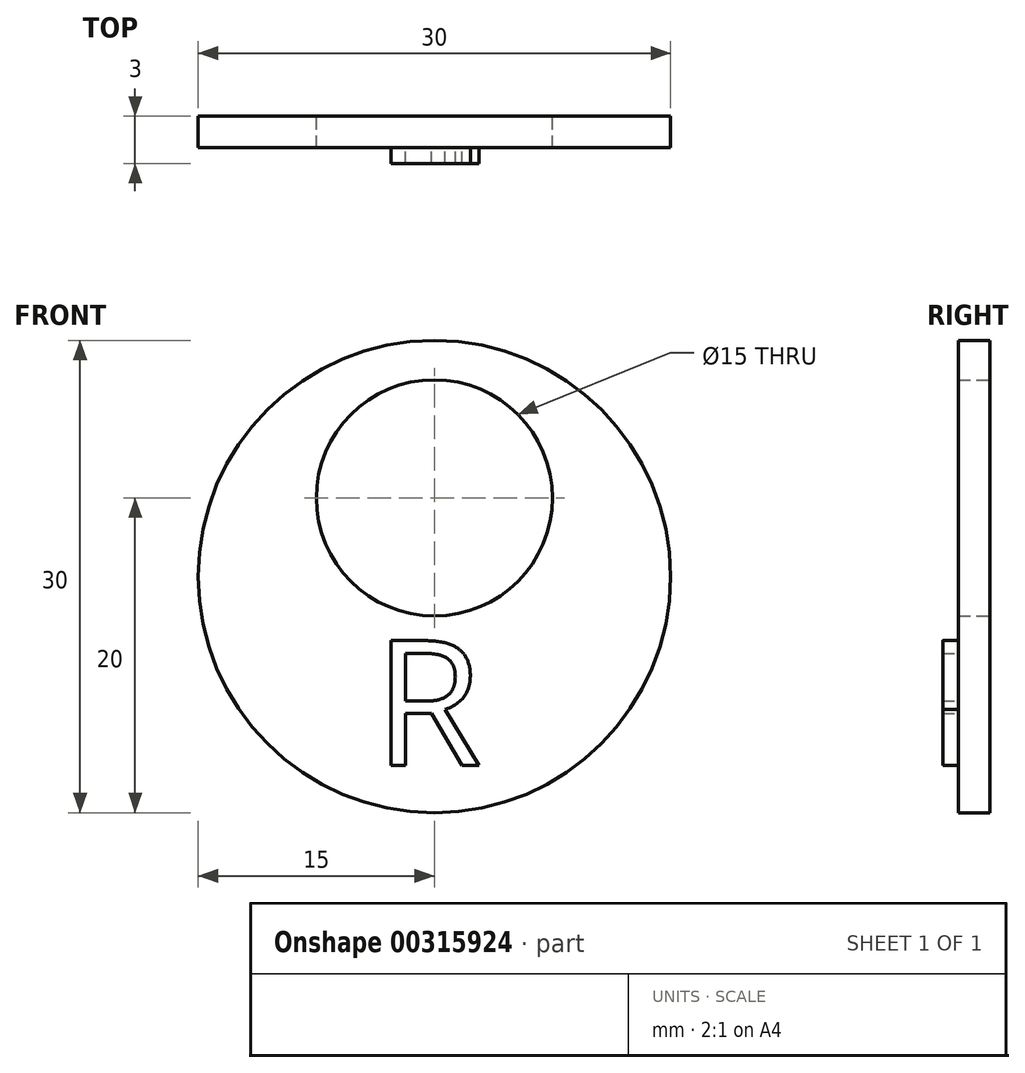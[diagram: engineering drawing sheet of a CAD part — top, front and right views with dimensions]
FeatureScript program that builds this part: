
annotation { "Feature Type Name" : "Feature", "Feature Type Description" : "" }
export const myFeature = defineFeature(function(context is Context, id is Id, definition is map)
    precondition{}
    {
        {
            var Q0;
            Q0=qCreatedBy(makeId("Front.planeOp"),FACE);
            var sketch = newSketch(context, id + "F0", { "sketchPlane" : qUnion([Q0])});
            skCircle(sketch, "E0", {"center": v(0, 0) * mm, "radius": 15 * mm});
            skPoint(sketch, "E1", {"position": v(0, 5) * mm});
            skCircle(sketch, "E2", {"center": v(0, 5) * mm, "radius": 7.5 * mm});
            skSolve(sketch);
        }
        {
            var Q0;
            Q0=makeQuery(id+"F0.imprint","IMPRINT",FACE,{"disambiguationData":[TD([[makeQuery(id+"F0.imprint","IMPRINT",EDGE,{"derivedFrom":sQuery(id+"F0.wireOp",EDGE,"E0")}),1.0]])]});
            extrude(context, id + "F1", {"entities" : qUnion([Q0]), "depth" : 2 * mm});
        }
        {
            var Q0;
            Q0=makeQuery(id+"F1.opExtrude","CAP_FACE",FACE,{"disambiguationData":[OSD([sQuery(id+"F0.wireOp",EDGE,"E0"),sQuery(id+"F0.wireOp",EDGE,"E2")])],"isStart":false});
            var sketch = newSketch(context, id + "F2", { "sketchPlane" : qUnion([Q0])});
            skText(sketch, "E3", { "text": "R\n", "fontName": "OpenSans-Regular.ttf"});
            const initialGuessF2  = {"E3": [-0.00384, -0.012, 1, 0, 0.008]};
            skSetInitialGuess(sketch, initialGuessF2);
            skSolve(sketch);
        }
        {
            var Q0;
            Q0 = qSketchRegion(id + "F2", true);
            extrude(context, id + "F3", {"entities" : qUnion([Q0]), "operationType" : NewBodyOperationType.ADD, "depth" : 1 * mm});
        }
    });
